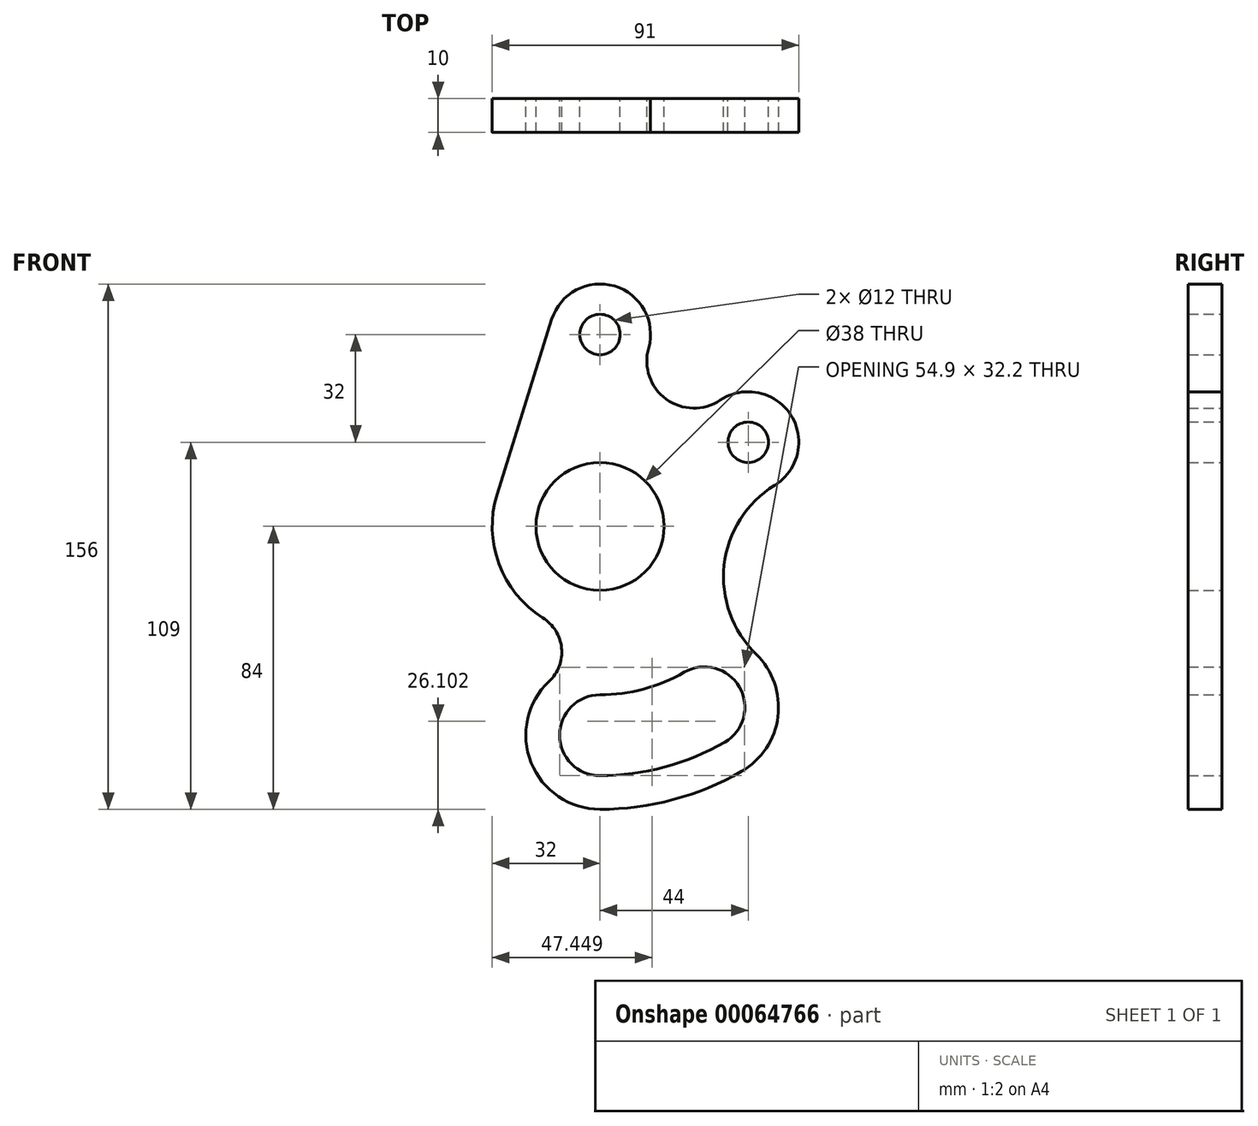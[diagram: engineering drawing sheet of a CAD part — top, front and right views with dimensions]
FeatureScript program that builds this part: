
annotation { "Feature Type Name" : "Feature", "Feature Type Description" : "" }
export const myFeature = defineFeature(function(context is Context, id is Id, definition is map)
    precondition{}
    {
        {
            var Q0;
            Q0=qCreatedBy(makeId("Front.planeOp"),FACE);
            var sketch = newSketch(context, id + "F0", { "sketchPlane" : qUnion([Q0])});
            skCircle(sketch, "E0", {"center": v(0, 0) * mm, "radius": 19 * mm});
            skCircle(sketch, "E1", {"center": v(0, 57) * mm, "radius": 6 * mm});
            skCircle(sketch, "E2", {"center": v(44, 25) * mm, "radius": 6 * mm});
            skArc(sketch, "E3", {"start": v(14.44, 52.93) * mm, "mid": v(4.27, 71.38) * mm, "end": v(-14.32, 61.47) * mm});
            skArc(sketch, "E4", {"start": v(51.87, 12.23) * mm, "mid": v(56.63, 33.1) * mm, "end": v(35.68, 37.48) * mm});
            skArc(sketch, "E5", {"start": v(-30.54, 9.54) * mm, "mid": v(-30.01, -11.1) * mm, "end": v(-16.99, -27.12) * mm});
            skLineSegment(sketch, "E6", {"start": v(-14.32, 61.47) * mm, "end": v(-30.54, 9.54) * mm});
            skArc(sketch, "E7", {"start": v(14.44, 52.93) * mm, "mid": v(19.68, 37.8) * mm, "end": v(35.68, 37.48) * mm});
            skArc(sketch, "E8", {"start": v(0, -50) * mm, "mid": v(-12, -62) * mm, "end": v(0, -74) * mm});
            skLineSegment(sketch, "E9", {"start": v(0, 0) * mm, "end": v(31, -53.7) * mm, "construction": true});
            skArc(sketch, "E10", {"start": v(37, -64.09) * mm, "mid": v(41.4, -47.7) * mm, "end": v(25, -43.3) * mm});
            skLineSegment(sketch, "E11", {"start": v(0, 0) * mm, "end": v(0, -62) * mm, "construction": true});
            skArc(sketch, "E12", {"start": v(0, -50) * mm, "mid": v(12.94, -48.3) * mm, "end": v(25, -43.3) * mm});
            skArc(sketch, "E13", {"start": v(0, -74) * mm, "mid": v(19.15, -71.48) * mm, "end": v(37, -64.09) * mm});
            skArc(sketch, "E14", {"start": v(-15.11, -46.01) * mm, "mid": v(-20.44, -70.13) * mm, "end": v(0, -84) * mm});
            skArc(sketch, "E15", {"start": v(0, -84) * mm, "mid": v(21.74, -81.14) * mm, "end": v(42, -72.75) * mm});
            skArc(sketch, "E16", {"start": v(-15.11, -46.01) * mm, "mid": v(-11.41, -36.1) * mm, "end": v(-16.99, -27.12) * mm});
            skArc(sketch, "E17", {"start": v(51.87, 12.23) * mm, "mid": v(36.86, -11.5) * mm, "end": v(46.35, -37.93) * mm});
            skArc(sketch, "E18.trimOffspring", {"start": v(42, -72.75) * mm, "mid": v(52.83, -56.42) * mm, "end": v(46.35, -37.93) * mm});
            skSolve(sketch);
        }
        {
            var Q0;
            Q0=makeQuery(id+"F0.imprint","IMPRINT",FACE,{"disambiguationData":[TD([[makeQuery(id+"F0.imprint","IMPRINT",EDGE,{"derivedFrom":sQuery(id+"F0.wireOp",EDGE,"E0")}),-1.0]])]});
            extrude(context, id + "F1", {"entities" : qUnion([Q0]), "flatOperationType" : FlatOperationType.REMOVE, "offsetDistance" : 25 * mm, "depth" : 10 * mm, "domain" : OperationDomain.MODEL});
        }
    });
